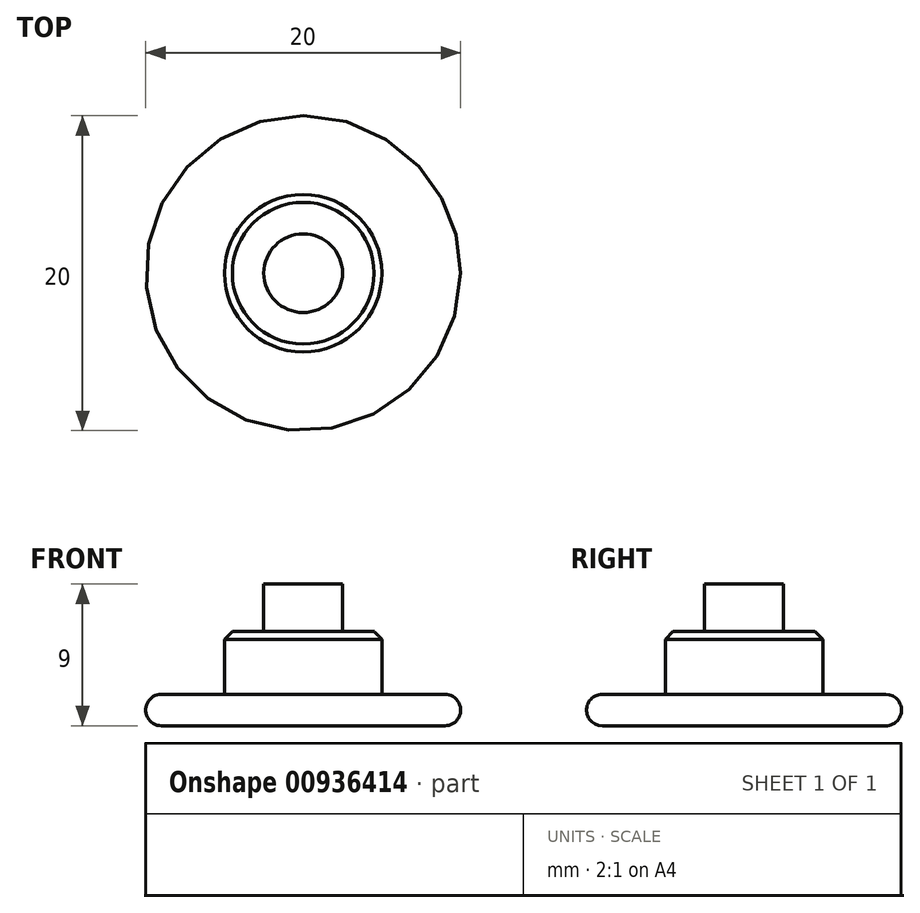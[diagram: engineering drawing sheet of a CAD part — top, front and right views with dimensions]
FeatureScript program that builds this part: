
annotation { "Feature Type Name" : "Feature", "Feature Type Description" : "" }
export const myFeature = defineFeature(function(context is Context, id is Id, definition is map)
    precondition{}
    {
        {
            var Q0;
            Q0=qCreatedBy(makeId("Top.planeOp"),FACE);
            var sketch = newSketch(context, id + "F0", { "sketchPlane" : qUnion([Q0])});
            skCircle(sketch, "E0", {"center": v(0, 0) * mm, "radius": 10 * mm});
            skSolve(sketch);
        }
        {
            var Q0;
            Q0 = qSketchRegion(id + "F0", true);
            extrude(context, id + "F1", {"entities" : qUnion([Q0]), "depth" : 2 * mm, "offsetDistance" : 25 * mm});
        }
        {
            var Q0;
            Q0=makeQuery(id+"F1.opExtrude","CAP_FACE",FACE,{"disambiguationData":[OSD([sQuery(id+"F0.wireOp",EDGE,"E0")])],"isStart":false});
            var sketch = newSketch(context, id + "F2", { "sketchPlane" : qUnion([Q0])});
            skCircle(sketch, "E1", {"center": v(0, 0) * mm, "radius": 5 * mm});
            skSolve(sketch);
        }
        {
            var Q0;
            Q0 = qSketchRegion(id + "F2", true);
            extrude(context, id + "F3", {"entities" : qUnion([Q0]), "operationType" : NewBodyOperationType.ADD, "depth" : 4 * mm, "offsetDistance" : 25 * mm});
        }
        {
            var Q0;
            Q0=makeQuery(id+"F3.opExtrude","CAP_EDGE",EDGE,{"disambiguationData":[OSD([sQuery(id+"F2.wireOp",EDGE,"E1")])],"isStart":false});
            chamfer(context, id + "F4", {"entities" : qUnion([Q0]), "width" : .5 * mm, "tangentPropagation" : true});
        }
        {
            var Q0;
            Q0=makeQuery(id+"F1.opExtrude","CAP_EDGE",EDGE,{"disambiguationData":[OSD([sQuery(id+"F0.wireOp",EDGE,"E0")])],"isStart":true});
            var Q1;
            Q1=makeQuery(id+"F1.opExtrude","CAP_EDGE",EDGE,{"disambiguationData":[OSD([sQuery(id+"F0.wireOp",EDGE,"E0")])],"isStart":false});
            fillet(context, id + "F5", {"entities" : qUnion([Q0, Q1]), "radius" : 1 * mm, "tangentPropagation" : true, "allowEdgeOverflow" : false});
        }
        {
            var Q0;
            Q0=makeQuery(id+"F3.opExtrude","CAP_FACE",FACE,{"disambiguationData":[OSD([sQuery(id+"F2.wireOp",EDGE,"E1")])],"isStart":false});
            var sketch = newSketch(context, id + "F6", { "sketchPlane" : qUnion([Q0])});
            skCircle(sketch, "E2", {"center": v(0, 0) * mm, "radius": 2.5 * mm});
            skSolve(sketch);
        }
        {
            var Q0;
            Q0 = qSketchRegion(id + "F6", true);
            extrude(context, id + "F7", {"entities" : qUnion([Q0]), "operationType" : NewBodyOperationType.ADD, "depth" : 3 * mm, "offsetDistance" : 25 * mm});
        }
    });
